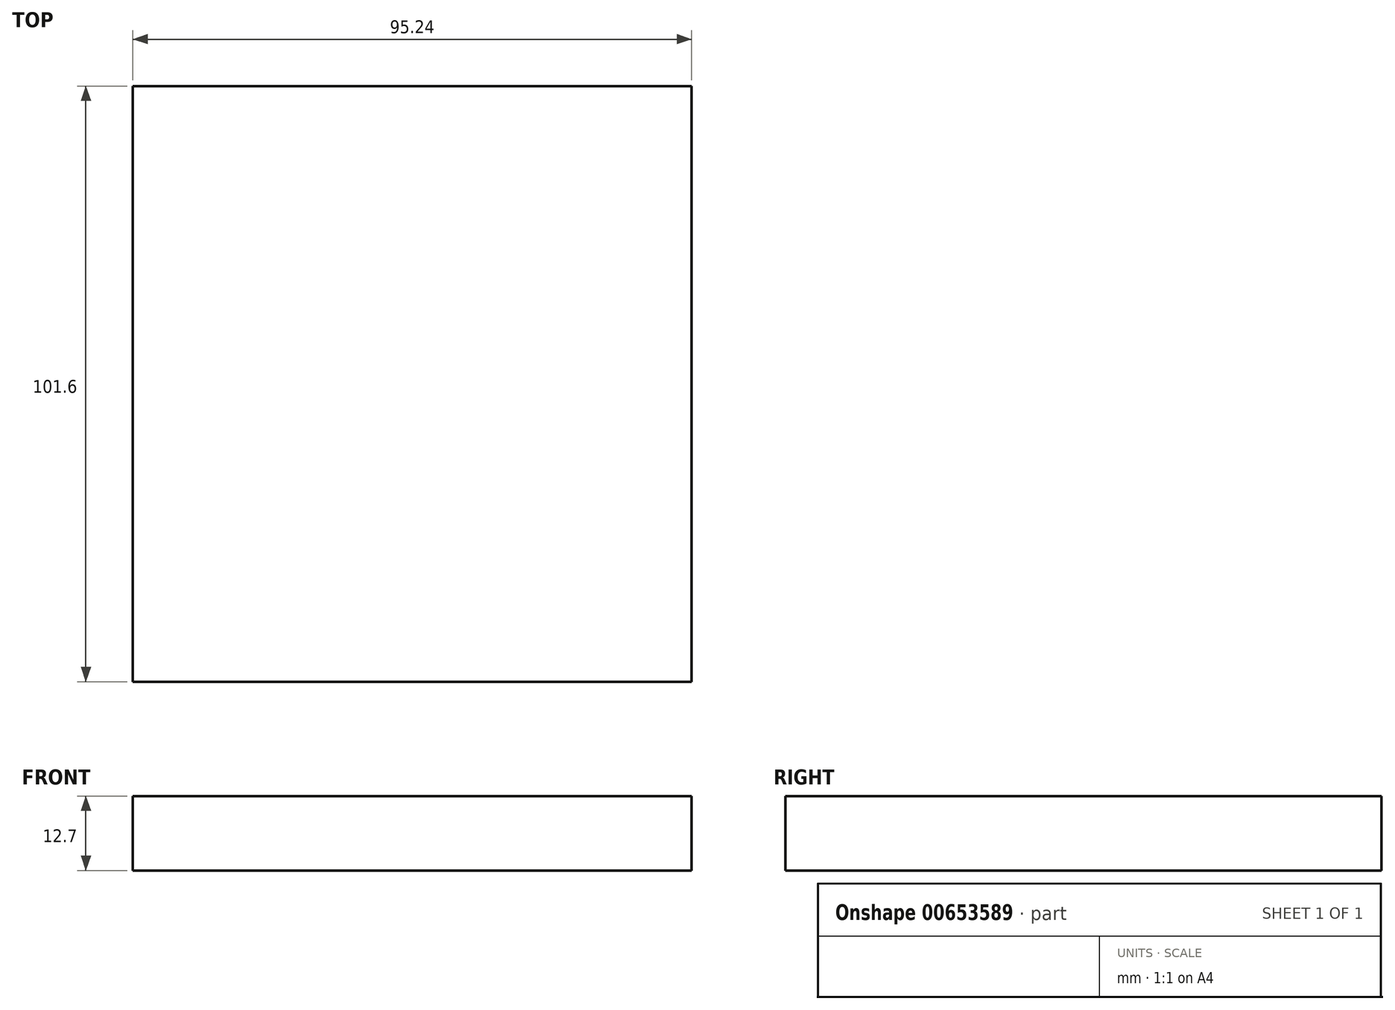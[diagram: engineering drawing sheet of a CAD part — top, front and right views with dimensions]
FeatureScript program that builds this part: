
annotation { "Feature Type Name" : "Feature", "Feature Type Description" : "" }
export const myFeature = defineFeature(function(context is Context, id is Id, definition is map)
    precondition{}
    {
        {
            var Q0;
            Q0=qCreatedBy(makeId("Top.planeOp"),FACE);
            var sketch = newSketch(context, id + "F0", { "sketchPlane" : qUnion([Q0])});
            skLineSegment(sketch, "E0.bottom", {"start": v(47.62, 50.8) * mm, "end": v(-47.63, 50.8) * mm});
            skLineSegment(sketch, "E0.top", {"start": v(47.63, -50.8) * mm, "end": v(-47.62, -50.8) * mm});
            skLineSegment(sketch, "E0.left", {"start": v(47.62, 50.8) * mm, "end": v(47.63, -50.8) * mm});
            skLineSegment(sketch, "E0.right", {"start": v(-47.63, 50.8) * mm, "end": v(-47.62, -50.8) * mm});
            skPoint(sketch, "E0.middle", {"position": v(0, 0) * mm});
            skSolve(sketch);
        }
        {
            var Q0;
            Q0=makeQuery(id+"F0.imprint","IMPRINT",FACE,{"disambiguationData":[TD([[makeQuery(id+"F0.imprint","IMPRINT",EDGE,{"derivedFrom":sQuery(id+"F0.wireOp",EDGE,"E0.bottom")}),1.0]])]});
            extrude(context, id + "F1", {"entities" : qUnion([Q0]), "depth" : 12.7 * mm, "offsetDistance" : 25.4 * mm});
        }
    });
